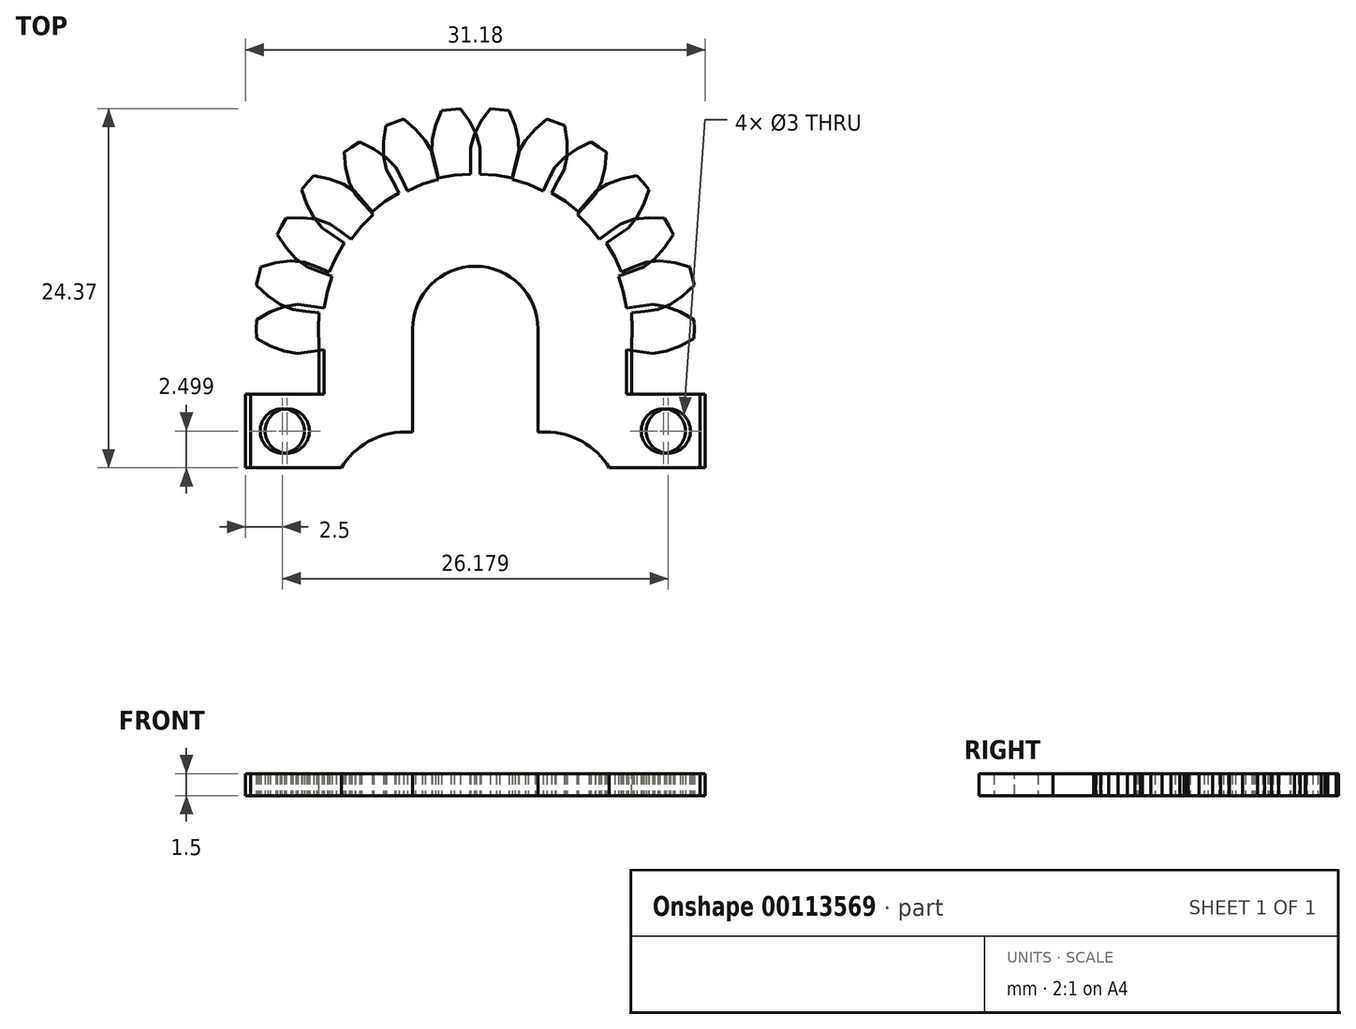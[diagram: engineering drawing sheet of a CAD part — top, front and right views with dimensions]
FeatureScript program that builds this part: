
annotation { "Feature Type Name" : "Feature", "Feature Type Description" : "" }
export const myFeature = defineFeature(function(context is Context, id is Id, definition is map)
    precondition{}
    {
        {
            var Q0;
            Q0=qCreatedBy(makeId("Top.planeOp"),FACE);
            var sketch = newSketch(context, id + "F0", { "sketchPlane" : qUnion([Q0])});
            skLineSegment(sketch, "E0", {"start": v(10.65, 0) * mm, "end": v(10.59, 1.11) * mm});
            skLineSegment(sketch, "E1", {"start": v(10.59, 1.11) * mm, "end": v(11.48, 1.2) * mm});
            skLineSegment(sketch, "E2", {"start": v(11.48, 1.2) * mm, "end": v(12.38, 1.3) * mm});
            skLineSegment(sketch, "E3", {"start": v(12.38, 1.3) * mm, "end": v(13.24, 1.67) * mm});
            skLineSegment(sketch, "E4", {"start": v(13.24, 1.67) * mm, "end": v(14.07, 2.24) * mm});
            skLineSegment(sketch, "E5", {"start": v(14.07, 2.24) * mm, "end": v(14.85, 2.97) * mm});
            skLineSegment(sketch, "E6", {"start": v(14.85, 2.97) * mm, "end": v(14.71, 3.59) * mm});
            skLineSegment(sketch, "E7", {"start": v(14.71, 3.59) * mm, "end": v(14.55, 4.2) * mm});
            skLineSegment(sketch, "E8", {"start": v(14.55, 4.2) * mm, "end": v(13.52, 4.49) * mm});
            skLineSegment(sketch, "E9", {"start": v(13.52, 4.49) * mm, "end": v(12.52, 4.6) * mm});
            skLineSegment(sketch, "E10", {"start": v(12.52, 4.6) * mm, "end": v(11.59, 4.53) * mm});
            skLineSegment(sketch, "E11", {"start": v(11.59, 4.53) * mm, "end": v(10.75, 4.2) * mm});
            skLineSegment(sketch, "E12", {"start": v(10.75, 4.2) * mm, "end": v(9.9, 3.87) * mm});
            skLineSegment(sketch, "E13", {"start": v(9.9, 3.87) * mm, "end": v(9.45, 4.88) * mm});
            skLineSegment(sketch, "E14", {"start": v(9.45, 4.88) * mm, "end": v(8.88, 5.84) * mm});
            skLineSegment(sketch, "E15", {"start": v(8.88, 5.84) * mm, "end": v(9.63, 6.34) * mm});
            skLineSegment(sketch, "E16", {"start": v(9.63, 6.34) * mm, "end": v(10.37, 6.84) * mm});
            skLineSegment(sketch, "E17", {"start": v(10.37, 6.84) * mm, "end": v(10.97, 7.56) * mm});
            skLineSegment(sketch, "E18", {"start": v(10.97, 7.56) * mm, "end": v(11.43, 8.45) * mm});
            skLineSegment(sketch, "E19", {"start": v(11.43, 8.45) * mm, "end": v(11.79, 9.46) * mm});
            skLineSegment(sketch, "E20", {"start": v(11.79, 9.46) * mm, "end": v(11.38, 9.95) * mm});
            skLineSegment(sketch, "E21", {"start": v(11.38, 9.95) * mm, "end": v(10.95, 10.41) * mm});
            skLineSegment(sketch, "E22", {"start": v(10.95, 10.41) * mm, "end": v(9.9, 10.19) * mm});
            skLineSegment(sketch, "E23", {"start": v(9.9, 10.19) * mm, "end": v(8.96, 9.83) * mm});
            skLineSegment(sketch, "E24", {"start": v(8.96, 9.83) * mm, "end": v(8.17, 9.32) * mm});
            skLineSegment(sketch, "E25", {"start": v(8.17, 9.32) * mm, "end": v(7.58, 8.64) * mm});
            skLineSegment(sketch, "E26", {"start": v(7.58, 8.64) * mm, "end": v(7, 7.96) * mm});
            skLineSegment(sketch, "E27", {"start": v(7, 7.96) * mm, "end": v(6.11, 8.64) * mm});
            skLineSegment(sketch, "E28", {"start": v(6.11, 8.64) * mm, "end": v(5.17, 9.22) * mm});
            skLineSegment(sketch, "E29", {"start": v(5.17, 9.22) * mm, "end": v(5.6, 10.01) * mm});
            skLineSegment(sketch, "E30", {"start": v(5.6, 10.01) * mm, "end": v(6.02, 10.8) * mm});
            skLineSegment(sketch, "E31", {"start": v(6.02, 10.8) * mm, "end": v(6.21, 11.72) * mm});
            skLineSegment(sketch, "E32", {"start": v(6.21, 11.72) * mm, "end": v(6.21, 12.73) * mm});
            skLineSegment(sketch, "E33", {"start": v(6.21, 12.73) * mm, "end": v(6.06, 13.79) * mm});
            skLineSegment(sketch, "E34", {"start": v(6.06, 13.79) * mm, "end": v(5.47, 14.03) * mm});
            skLineSegment(sketch, "E35", {"start": v(5.47, 14.03) * mm, "end": v(4.87, 14.24) * mm});
            skLineSegment(sketch, "E36", {"start": v(4.87, 14.24) * mm, "end": v(4.05, 13.55) * mm});
            skLineSegment(sketch, "E37", {"start": v(4.05, 13.55) * mm, "end": v(3.38, 12.8) * mm});
            skLineSegment(sketch, "E38", {"start": v(3.38, 12.8) * mm, "end": v(2.92, 11.98) * mm});
            skLineSegment(sketch, "E39", {"start": v(2.92, 11.98) * mm, "end": v(2.71, 11.1) * mm});
            skLineSegment(sketch, "E40", {"start": v(2.71, 11.1) * mm, "end": v(2.5, 10.23) * mm});
            skLineSegment(sketch, "E41", {"start": v(2.5, 10.23) * mm, "end": v(1.41, 10.42) * mm});
            skLineSegment(sketch, "E42", {"start": v(1.41, 10.42) * mm, "end": v(0.3, 10.5) * mm});
            skLineSegment(sketch, "E43", {"start": v(0.3, 10.5) * mm, "end": v(0.32, 11.4) * mm});
            skLineSegment(sketch, "E44", {"start": v(0.32, 11.4) * mm, "end": v(0.33, 12.3) * mm});
            skLineSegment(sketch, "E45", {"start": v(0.33, 12.3) * mm, "end": v(0.07, 13.2) * mm});
            skLineSegment(sketch, "E46", {"start": v(0.07, 13.2) * mm, "end": v(-0.4, 14.09) * mm});
            skLineSegment(sketch, "E47", {"start": v(-0.4, 14.09) * mm, "end": v(-1.03, 14.95) * mm});
            skLineSegment(sketch, "E48", {"start": v(-1.03, 14.95) * mm, "end": v(-1.66, 14.9) * mm});
            skLineSegment(sketch, "E49", {"start": v(-1.66, 14.9) * mm, "end": v(-2.29, 14.8) * mm});
            skLineSegment(sketch, "E50", {"start": v(-2.29, 14.8) * mm, "end": v(-2.7, 13.81) * mm});
            skLineSegment(sketch, "E51", {"start": v(-2.7, 13.81) * mm, "end": v(-2.93, 12.83) * mm});
            skLineSegment(sketch, "E52", {"start": v(-2.93, 12.83) * mm, "end": v(-2.97, 11.9) * mm});
            skLineSegment(sketch, "E53", {"start": v(-2.97, 11.9) * mm, "end": v(-2.74, 11.03) * mm});
            skLineSegment(sketch, "E54", {"start": v(-2.74, 11.03) * mm, "end": v(-2.52, 10.16) * mm});
            skLineSegment(sketch, "E55", {"start": v(-2.52, 10.16) * mm, "end": v(-3.57, 9.82) * mm});
            skLineSegment(sketch, "E56", {"start": v(-3.57, 9.82) * mm, "end": v(-4.6, 9.37) * mm});
            skLineSegment(sketch, "E57", {"start": v(-4.6, 9.37) * mm, "end": v(-5, 10.17) * mm});
            skLineSegment(sketch, "E58", {"start": v(-5, 10.17) * mm, "end": v(-5.41, 10.97) * mm});
            skLineSegment(sketch, "E59", {"start": v(-5.41, 10.97) * mm, "end": v(-6.05, 11.65) * mm});
            skLineSegment(sketch, "E60", {"start": v(-6.05, 11.65) * mm, "end": v(-6.88, 12.22) * mm});
            skLineSegment(sketch, "E61", {"start": v(-6.88, 12.22) * mm, "end": v(-7.84, 12.7) * mm});
            skLineSegment(sketch, "E62", {"start": v(-7.84, 12.7) * mm, "end": v(-8.37, 12.34) * mm});
            skLineSegment(sketch, "E63", {"start": v(-8.37, 12.34) * mm, "end": v(-8.89, 11.97) * mm});
            skLineSegment(sketch, "E64", {"start": v(-8.89, 11.97) * mm, "end": v(-8.79, 10.9) * mm});
            skLineSegment(sketch, "E65", {"start": v(-8.79, 10.9) * mm, "end": v(-8.55, 9.93) * mm});
            skLineSegment(sketch, "E66", {"start": v(-8.55, 9.93) * mm, "end": v(-8.14, 9.09) * mm});
            skLineSegment(sketch, "E67", {"start": v(-8.14, 9.09) * mm, "end": v(-7.54, 8.42) * mm});
            skLineSegment(sketch, "E68", {"start": v(-7.54, 8.42) * mm, "end": v(-6.93, 7.75) * mm});
            skLineSegment(sketch, "E69", {"start": v(-6.93, 7.75) * mm, "end": v(-7.71, 6.96) * mm});
            skLineSegment(sketch, "E70", {"start": v(-7.71, 6.96) * mm, "end": v(-8.4, 6.1) * mm});
            skLineSegment(sketch, "E71", {"start": v(-8.4, 6.1) * mm, "end": v(-9.14, 6.62) * mm});
            skLineSegment(sketch, "E72", {"start": v(-9.14, 6.62) * mm, "end": v(-9.87, 7.13) * mm});
            skLineSegment(sketch, "E73", {"start": v(-9.87, 7.13) * mm, "end": v(-10.76, 7.43) * mm});
            skLineSegment(sketch, "E74", {"start": v(-10.76, 7.43) * mm, "end": v(-11.76, 7.56) * mm});
            skLineSegment(sketch, "E75", {"start": v(-11.76, 7.56) * mm, "end": v(-12.83, 7.53) * mm});
            skLineSegment(sketch, "E76", {"start": v(-12.83, 7.53) * mm, "end": v(-13.13, 6.97) * mm});
            skLineSegment(sketch, "E77", {"start": v(-13.13, 6.97) * mm, "end": v(-13.42, 6.4) * mm});
            skLineSegment(sketch, "E78", {"start": v(-13.42, 6.4) * mm, "end": v(-12.83, 5.5) * mm});
            skLineSegment(sketch, "E79", {"start": v(-12.83, 5.5) * mm, "end": v(-12.17, 4.75) * mm});
            skLineSegment(sketch, "E80", {"start": v(-12.17, 4.75) * mm, "end": v(-11.41, 4.2) * mm});
            skLineSegment(sketch, "E81", {"start": v(-11.41, 4.2) * mm, "end": v(-10.57, 3.88) * mm});
            skLineSegment(sketch, "E82", {"start": v(-10.57, 3.88) * mm, "end": v(-9.72, 3.58) * mm});
            skLineSegment(sketch, "E83", {"start": v(-9.72, 3.58) * mm, "end": v(-10.05, 2.51) * mm});
            skLineSegment(sketch, "E84", {"start": v(-10.05, 2.51) * mm, "end": v(-10.25, 1.42) * mm});
            skLineSegment(sketch, "E85", {"start": v(-10.25, 1.42) * mm, "end": v(-11.15, 1.54) * mm});
            skLineSegment(sketch, "E86", {"start": v(-11.15, 1.54) * mm, "end": v(-12.04, 1.66) * mm});
            skLineSegment(sketch, "E87", {"start": v(-12.04, 1.66) * mm, "end": v(-12.96, 1.51) * mm});
            skLineSegment(sketch, "E88", {"start": v(-12.96, 1.51) * mm, "end": v(-13.9, 1.16) * mm});
            skLineSegment(sketch, "E89", {"start": v(-13.9, 1.16) * mm, "end": v(-14.84, 0.63) * mm});
            skLineSegment(sketch, "E90", {"start": v(-14.84, 0.63) * mm, "end": v(-14.85, 0) * mm});
            skLineSegment(sketch, "E91", {"start": v(-14.85, 0) * mm, "end": v(-14.84, -0.63) * mm});
            skLineSegment(sketch, "E92", {"start": v(-14.84, -0.63) * mm, "end": v(-13.9, -1.16) * mm});
            skLineSegment(sketch, "E93", {"start": v(-13.9, -1.16) * mm, "end": v(-12.96, -1.51) * mm});
            skLineSegment(sketch, "E94", {"start": v(-12.96, -1.51) * mm, "end": v(-12.04, -1.66) * mm});
            skLineSegment(sketch, "E95", {"start": v(-12.04, -1.66) * mm, "end": v(-11.15, -1.54) * mm});
            skLineSegment(sketch, "E96", {"start": v(-11.15, -1.54) * mm, "end": v(-10.25, -1.42) * mm});
            skLineSegment(sketch, "E97", {"start": v(-10.25, -1.42) * mm, "end": v(-10.05, -2.51) * mm});
            skLineSegment(sketch, "E98", {"start": v(-10.05, -2.51) * mm, "end": v(-9.72, -3.58) * mm});
            skLineSegment(sketch, "E99", {"start": v(-9.72, -3.58) * mm, "end": v(-10.57, -3.88) * mm});
            skLineSegment(sketch, "E100", {"start": v(-10.57, -3.88) * mm, "end": v(-11.41, -4.2) * mm});
            skLineSegment(sketch, "E101", {"start": v(-11.41, -4.2) * mm, "end": v(-12.17, -4.75) * mm});
            skLineSegment(sketch, "E102", {"start": v(-12.17, -4.75) * mm, "end": v(-12.83, -5.5) * mm});
            skLineSegment(sketch, "E103", {"start": v(-12.83, -5.5) * mm, "end": v(-13.42, -6.4) * mm});
            skLineSegment(sketch, "E104", {"start": v(-13.42, -6.4) * mm, "end": v(-13.13, -6.97) * mm});
            skLineSegment(sketch, "E105", {"start": v(-13.13, -6.97) * mm, "end": v(-12.83, -7.53) * mm});
            skLineSegment(sketch, "E106", {"start": v(-12.83, -7.53) * mm, "end": v(-11.76, -7.56) * mm});
            skLineSegment(sketch, "E107", {"start": v(-11.76, -7.56) * mm, "end": v(-10.76, -7.43) * mm});
            skLineSegment(sketch, "E108", {"start": v(-10.76, -7.43) * mm, "end": v(-9.87, -7.13) * mm});
            skLineSegment(sketch, "E109", {"start": v(-9.87, -7.13) * mm, "end": v(-9.14, -6.62) * mm});
            skLineSegment(sketch, "E110", {"start": v(-9.14, -6.62) * mm, "end": v(-8.4, -6.1) * mm});
            skLineSegment(sketch, "E111", {"start": v(-8.4, -6.1) * mm, "end": v(-7.71, -6.96) * mm});
            skLineSegment(sketch, "E112", {"start": v(-7.71, -6.96) * mm, "end": v(-6.93, -7.75) * mm});
            skLineSegment(sketch, "E113", {"start": v(-6.93, -7.75) * mm, "end": v(-7.54, -8.42) * mm});
            skLineSegment(sketch, "E114", {"start": v(-7.54, -8.42) * mm, "end": v(-8.14, -9.09) * mm});
            skLineSegment(sketch, "E115", {"start": v(-8.14, -9.09) * mm, "end": v(-8.55, -9.93) * mm});
            skLineSegment(sketch, "E116", {"start": v(-8.55, -9.93) * mm, "end": v(-8.79, -10.9) * mm});
            skLineSegment(sketch, "E117", {"start": v(-8.79, -10.9) * mm, "end": v(-8.89, -11.97) * mm});
            skLineSegment(sketch, "E118", {"start": v(-8.89, -11.97) * mm, "end": v(-8.37, -12.34) * mm});
            skLineSegment(sketch, "E119", {"start": v(-8.37, -12.34) * mm, "end": v(-7.84, -12.7) * mm});
            skLineSegment(sketch, "E120", {"start": v(-7.84, -12.7) * mm, "end": v(-6.88, -12.22) * mm});
            skLineSegment(sketch, "E121", {"start": v(-6.88, -12.22) * mm, "end": v(-6.05, -11.65) * mm});
            skLineSegment(sketch, "E122", {"start": v(-6.05, -11.65) * mm, "end": v(-5.41, -10.97) * mm});
            skLineSegment(sketch, "E123", {"start": v(-5.41, -10.97) * mm, "end": v(-5, -10.17) * mm});
            skLineSegment(sketch, "E124", {"start": v(-5, -10.17) * mm, "end": v(-4.6, -9.37) * mm});
            skLineSegment(sketch, "E125", {"start": v(-4.6, -9.37) * mm, "end": v(-3.57, -9.82) * mm});
            skLineSegment(sketch, "E126", {"start": v(-3.57, -9.82) * mm, "end": v(-2.52, -10.16) * mm});
            skLineSegment(sketch, "E127", {"start": v(-2.52, -10.16) * mm, "end": v(-2.74, -11.03) * mm});
            skLineSegment(sketch, "E128", {"start": v(-2.74, -11.03) * mm, "end": v(-2.97, -11.9) * mm});
            skLineSegment(sketch, "E129", {"start": v(-2.97, -11.9) * mm, "end": v(-2.93, -12.83) * mm});
            skLineSegment(sketch, "E130", {"start": v(-2.93, -12.83) * mm, "end": v(-2.7, -13.81) * mm});
            skLineSegment(sketch, "E131", {"start": v(-2.7, -13.81) * mm, "end": v(-2.29, -14.8) * mm});
            skLineSegment(sketch, "E132", {"start": v(-2.29, -14.8) * mm, "end": v(-1.66, -14.9) * mm});
            skLineSegment(sketch, "E133", {"start": v(-1.66, -14.9) * mm, "end": v(-1.03, -14.95) * mm});
            skLineSegment(sketch, "E134", {"start": v(-1.03, -14.95) * mm, "end": v(-0.4, -14.09) * mm});
            skLineSegment(sketch, "E135", {"start": v(-0.4, -14.09) * mm, "end": v(0.07, -13.2) * mm});
            skLineSegment(sketch, "E136", {"start": v(0.07, -13.2) * mm, "end": v(0.33, -12.3) * mm});
            skLineSegment(sketch, "E137", {"start": v(0.33, -12.3) * mm, "end": v(0.32, -11.4) * mm});
            skLineSegment(sketch, "E138", {"start": v(0.32, -11.4) * mm, "end": v(0.3, -10.5) * mm});
            skLineSegment(sketch, "E139", {"start": v(0.3, -10.5) * mm, "end": v(1.41, -10.42) * mm});
            skLineSegment(sketch, "E140", {"start": v(1.41, -10.42) * mm, "end": v(2.5, -10.23) * mm});
            skLineSegment(sketch, "E141", {"start": v(2.5, -10.23) * mm, "end": v(2.71, -11.1) * mm});
            skLineSegment(sketch, "E142", {"start": v(2.71, -11.1) * mm, "end": v(2.92, -11.98) * mm});
            skLineSegment(sketch, "E143", {"start": v(2.92, -11.98) * mm, "end": v(3.38, -12.8) * mm});
            skLineSegment(sketch, "E144", {"start": v(3.38, -12.8) * mm, "end": v(4.05, -13.55) * mm});
            skLineSegment(sketch, "E145", {"start": v(4.05, -13.55) * mm, "end": v(4.87, -14.24) * mm});
            skLineSegment(sketch, "E146", {"start": v(4.87, -14.24) * mm, "end": v(5.47, -14.03) * mm});
            skLineSegment(sketch, "E147", {"start": v(5.47, -14.03) * mm, "end": v(6.06, -13.79) * mm});
            skLineSegment(sketch, "E148", {"start": v(6.06, -13.79) * mm, "end": v(6.21, -12.73) * mm});
            skLineSegment(sketch, "E149", {"start": v(6.21, -12.73) * mm, "end": v(6.21, -11.72) * mm});
            skLineSegment(sketch, "E150", {"start": v(6.21, -11.72) * mm, "end": v(6.02, -10.8) * mm});
            skLineSegment(sketch, "E151", {"start": v(6.02, -10.8) * mm, "end": v(5.6, -10.01) * mm});
            skLineSegment(sketch, "E152", {"start": v(5.6, -10.01) * mm, "end": v(5.17, -9.22) * mm});
            skLineSegment(sketch, "E153", {"start": v(5.17, -9.22) * mm, "end": v(6.11, -8.64) * mm});
            skLineSegment(sketch, "E154", {"start": v(6.11, -8.64) * mm, "end": v(7, -7.96) * mm});
            skLineSegment(sketch, "E155", {"start": v(7, -7.96) * mm, "end": v(7.58, -8.64) * mm});
            skLineSegment(sketch, "E156", {"start": v(7.58, -8.64) * mm, "end": v(8.17, -9.32) * mm});
            skLineSegment(sketch, "E157", {"start": v(8.17, -9.32) * mm, "end": v(8.96, -9.83) * mm});
            skLineSegment(sketch, "E158", {"start": v(8.96, -9.83) * mm, "end": v(9.9, -10.19) * mm});
            skLineSegment(sketch, "E159", {"start": v(9.9, -10.19) * mm, "end": v(10.95, -10.41) * mm});
            skLineSegment(sketch, "E160", {"start": v(10.95, -10.41) * mm, "end": v(11.38, -9.95) * mm});
            skLineSegment(sketch, "E161", {"start": v(11.38, -9.95) * mm, "end": v(11.79, -9.46) * mm});
            skLineSegment(sketch, "E162", {"start": v(11.79, -9.46) * mm, "end": v(11.43, -8.45) * mm});
            skLineSegment(sketch, "E163", {"start": v(11.43, -8.45) * mm, "end": v(10.97, -7.56) * mm});
            skLineSegment(sketch, "E164", {"start": v(10.97, -7.56) * mm, "end": v(10.37, -6.84) * mm});
            skLineSegment(sketch, "E165", {"start": v(10.37, -6.84) * mm, "end": v(9.63, -6.34) * mm});
            skLineSegment(sketch, "E166", {"start": v(9.63, -6.34) * mm, "end": v(8.88, -5.84) * mm});
            skLineSegment(sketch, "E167", {"start": v(8.88, -5.84) * mm, "end": v(9.45, -4.88) * mm});
            skLineSegment(sketch, "E168", {"start": v(9.45, -4.88) * mm, "end": v(9.9, -3.87) * mm});
            skLineSegment(sketch, "E169", {"start": v(9.9, -3.87) * mm, "end": v(10.75, -4.2) * mm});
            skLineSegment(sketch, "E170", {"start": v(10.75, -4.2) * mm, "end": v(11.59, -4.53) * mm});
            skLineSegment(sketch, "E171", {"start": v(11.59, -4.53) * mm, "end": v(12.52, -4.6) * mm});
            skLineSegment(sketch, "E172", {"start": v(12.52, -4.6) * mm, "end": v(13.52, -4.49) * mm});
            skLineSegment(sketch, "E173", {"start": v(13.52, -4.49) * mm, "end": v(14.55, -4.2) * mm});
            skLineSegment(sketch, "E174", {"start": v(14.55, -4.2) * mm, "end": v(14.71, -3.59) * mm});
            skLineSegment(sketch, "E175", {"start": v(14.71, -3.59) * mm, "end": v(14.85, -2.97) * mm});
            skLineSegment(sketch, "E176", {"start": v(14.85, -2.97) * mm, "end": v(14.07, -2.24) * mm});
            skLineSegment(sketch, "E177", {"start": v(14.07, -2.24) * mm, "end": v(13.24, -1.67) * mm});
            skLineSegment(sketch, "E178", {"start": v(13.24, -1.67) * mm, "end": v(12.38, -1.3) * mm});
            skLineSegment(sketch, "E179", {"start": v(12.38, -1.3) * mm, "end": v(11.48, -1.2) * mm});
            skLineSegment(sketch, "E180", {"start": v(11.48, -1.2) * mm, "end": v(10.59, -1.11) * mm});
            skLineSegment(sketch, "E181", {"start": v(10.65, 0) * mm, "end": v(10.59, -1.11) * mm});
            skSolve(sketch);
        }
        {
            var Q0;
            Q0=qSketchRegion(id+"F0",true);
            extrude(context, id + "F1", {"entities" : qUnion([Q0]), "depth" : 1.5 * mm});
        }
        {
            var Q0;
            Q0=makeQuery(id+"F1.opExtrude","CAP_FACE",FACE,{"disambiguationData":[OSD([sQuery(id+"F0.wireOp",EDGE,"E0"),sQuery(id+"F0.wireOp",EDGE,"E1"),sQuery(id+"F0.wireOp",EDGE,"E2"),sQuery(id+"F0.wireOp",EDGE,"E3"),sQuery(id+"F0.wireOp",EDGE,"E4"),sQuery(id+"F0.wireOp",EDGE,"E5"),sQuery(id+"F0.wireOp",EDGE,"E6"),sQuery(id+"F0.wireOp",EDGE,"E7"),sQuery(id+"F0.wireOp",EDGE,"E8"),sQuery(id+"F0.wireOp",EDGE,"E9"),sQuery(id+"F0.wireOp",EDGE,"E10"),sQuery(id+"F0.wireOp",EDGE,"E11"),sQuery(id+"F0.wireOp",EDGE,"E12"),sQuery(id+"F0.wireOp",EDGE,"E13"),sQuery(id+"F0.wireOp",EDGE,"E14"),sQuery(id+"F0.wireOp",EDGE,"E15"),sQuery(id+"F0.wireOp",EDGE,"E16"),sQuery(id+"F0.wireOp",EDGE,"E17"),sQuery(id+"F0.wireOp",EDGE,"E18"),sQuery(id+"F0.wireOp",EDGE,"E19"),sQuery(id+"F0.wireOp",EDGE,"E20"),sQuery(id+"F0.wireOp",EDGE,"E21"),sQuery(id+"F0.wireOp",EDGE,"E22"),sQuery(id+"F0.wireOp",EDGE,"E23"),sQuery(id+"F0.wireOp",EDGE,"E24"),sQuery(id+"F0.wireOp",EDGE,"E25"),sQuery(id+"F0.wireOp",EDGE,"E26"),sQuery(id+"F0.wireOp",EDGE,"E27"),sQuery(id+"F0.wireOp",EDGE,"E28"),sQuery(id+"F0.wireOp",EDGE,"E29"),sQuery(id+"F0.wireOp",EDGE,"E30"),sQuery(id+"F0.wireOp",EDGE,"E31"),sQuery(id+"F0.wireOp",EDGE,"E32"),sQuery(id+"F0.wireOp",EDGE,"E33"),sQuery(id+"F0.wireOp",EDGE,"E34"),sQuery(id+"F0.wireOp",EDGE,"E35"),sQuery(id+"F0.wireOp",EDGE,"E36"),sQuery(id+"F0.wireOp",EDGE,"E37"),sQuery(id+"F0.wireOp",EDGE,"E38"),sQuery(id+"F0.wireOp",EDGE,"E39"),sQuery(id+"F0.wireOp",EDGE,"E40"),sQuery(id+"F0.wireOp",EDGE,"E41"),sQuery(id+"F0.wireOp",EDGE,"E42"),sQuery(id+"F0.wireOp",EDGE,"E43"),sQuery(id+"F0.wireOp",EDGE,"E44"),sQuery(id+"F0.wireOp",EDGE,"E45"),sQuery(id+"F0.wireOp",EDGE,"E46"),sQuery(id+"F0.wireOp",EDGE,"E47"),sQuery(id+"F0.wireOp",EDGE,"E48"),sQuery(id+"F0.wireOp",EDGE,"E49"),sQuery(id+"F0.wireOp",EDGE,"E50"),sQuery(id+"F0.wireOp",EDGE,"E51"),sQuery(id+"F0.wireOp",EDGE,"E52"),sQuery(id+"F0.wireOp",EDGE,"E53"),sQuery(id+"F0.wireOp",EDGE,"E54"),sQuery(id+"F0.wireOp",EDGE,"E55"),sQuery(id+"F0.wireOp",EDGE,"E56"),sQuery(id+"F0.wireOp",EDGE,"E57"),sQuery(id+"F0.wireOp",EDGE,"E58"),sQuery(id+"F0.wireOp",EDGE,"E59"),sQuery(id+"F0.wireOp",EDGE,"E60"),sQuery(id+"F0.wireOp",EDGE,"E61"),sQuery(id+"F0.wireOp",EDGE,"E62"),sQuery(id+"F0.wireOp",EDGE,"E63"),sQuery(id+"F0.wireOp",EDGE,"E64"),sQuery(id+"F0.wireOp",EDGE,"E65"),sQuery(id+"F0.wireOp",EDGE,"E66"),sQuery(id+"F0.wireOp",EDGE,"E67"),sQuery(id+"F0.wireOp",EDGE,"E68"),sQuery(id+"F0.wireOp",EDGE,"E69"),sQuery(id+"F0.wireOp",EDGE,"E70"),sQuery(id+"F0.wireOp",EDGE,"E71"),sQuery(id+"F0.wireOp",EDGE,"E72"),sQuery(id+"F0.wireOp",EDGE,"E73"),sQuery(id+"F0.wireOp",EDGE,"E74"),sQuery(id+"F0.wireOp",EDGE,"E75"),sQuery(id+"F0.wireOp",EDGE,"E76"),sQuery(id+"F0.wireOp",EDGE,"E77"),sQuery(id+"F0.wireOp",EDGE,"E78"),sQuery(id+"F0.wireOp",EDGE,"E79"),sQuery(id+"F0.wireOp",EDGE,"E80"),sQuery(id+"F0.wireOp",EDGE,"E81"),sQuery(id+"F0.wireOp",EDGE,"E82"),sQuery(id+"F0.wireOp",EDGE,"E83"),sQuery(id+"F0.wireOp",EDGE,"E84"),sQuery(id+"F0.wireOp",EDGE,"E85"),sQuery(id+"F0.wireOp",EDGE,"E86"),sQuery(id+"F0.wireOp",EDGE,"E87"),sQuery(id+"F0.wireOp",EDGE,"E88"),sQuery(id+"F0.wireOp",EDGE,"E89"),sQuery(id+"F0.wireOp",EDGE,"E90"),sQuery(id+"F0.wireOp",EDGE,"E91"),sQuery(id+"F0.wireOp",EDGE,"E92"),sQuery(id+"F0.wireOp",EDGE,"E93"),sQuery(id+"F0.wireOp",EDGE,"E94"),sQuery(id+"F0.wireOp",EDGE,"E95"),sQuery(id+"F0.wireOp",EDGE,"E96"),sQuery(id+"F0.wireOp",EDGE,"E97"),sQuery(id+"F0.wireOp",EDGE,"E98"),sQuery(id+"F0.wireOp",EDGE,"E99"),sQuery(id+"F0.wireOp",EDGE,"E100"),sQuery(id+"F0.wireOp",EDGE,"E101"),sQuery(id+"F0.wireOp",EDGE,"E102"),sQuery(id+"F0.wireOp",EDGE,"E103"),sQuery(id+"F0.wireOp",EDGE,"E104"),sQuery(id+"F0.wireOp",EDGE,"E105"),sQuery(id+"F0.wireOp",EDGE,"E106"),sQuery(id+"F0.wireOp",EDGE,"E107"),sQuery(id+"F0.wireOp",EDGE,"E108"),sQuery(id+"F0.wireOp",EDGE,"E109"),sQuery(id+"F0.wireOp",EDGE,"E110"),sQuery(id+"F0.wireOp",EDGE,"E111"),sQuery(id+"F0.wireOp",EDGE,"E112"),sQuery(id+"F0.wireOp",EDGE,"E113"),sQuery(id+"F0.wireOp",EDGE,"E114"),sQuery(id+"F0.wireOp",EDGE,"E115"),sQuery(id+"F0.wireOp",EDGE,"E116"),sQuery(id+"F0.wireOp",EDGE,"E117"),sQuery(id+"F0.wireOp",EDGE,"E118"),sQuery(id+"F0.wireOp",EDGE,"E119"),sQuery(id+"F0.wireOp",EDGE,"E120"),sQuery(id+"F0.wireOp",EDGE,"E121"),sQuery(id+"F0.wireOp",EDGE,"E122"),sQuery(id+"F0.wireOp",EDGE,"E123"),sQuery(id+"F0.wireOp",EDGE,"E124"),sQuery(id+"F0.wireOp",EDGE,"E125"),sQuery(id+"F0.wireOp",EDGE,"E126"),sQuery(id+"F0.wireOp",EDGE,"E127"),sQuery(id+"F0.wireOp",EDGE,"E128"),sQuery(id+"F0.wireOp",EDGE,"E129"),sQuery(id+"F0.wireOp",EDGE,"E130"),sQuery(id+"F0.wireOp",EDGE,"E131"),sQuery(id+"F0.wireOp",EDGE,"E132"),sQuery(id+"F0.wireOp",EDGE,"E133"),sQuery(id+"F0.wireOp",EDGE,"E134"),sQuery(id+"F0.wireOp",EDGE,"E135"),sQuery(id+"F0.wireOp",EDGE,"E136"),sQuery(id+"F0.wireOp",EDGE,"E137"),sQuery(id+"F0.wireOp",EDGE,"E138"),sQuery(id+"F0.wireOp",EDGE,"E139"),sQuery(id+"F0.wireOp",EDGE,"E140"),sQuery(id+"F0.wireOp",EDGE,"E141"),sQuery(id+"F0.wireOp",EDGE,"E142"),sQuery(id+"F0.wireOp",EDGE,"E143"),sQuery(id+"F0.wireOp",EDGE,"E144"),sQuery(id+"F0.wireOp",EDGE,"E145"),sQuery(id+"F0.wireOp",EDGE,"E146"),sQuery(id+"F0.wireOp",EDGE,"E147"),sQuery(id+"F0.wireOp",EDGE,"E148"),sQuery(id+"F0.wireOp",EDGE,"E149"),sQuery(id+"F0.wireOp",EDGE,"E150"),sQuery(id+"F0.wireOp",EDGE,"E151"),sQuery(id+"F0.wireOp",EDGE,"E152"),sQuery(id+"F0.wireOp",EDGE,"E153"),sQuery(id+"F0.wireOp",EDGE,"E154"),sQuery(id+"F0.wireOp",EDGE,"E155"),sQuery(id+"F0.wireOp",EDGE,"E156"),sQuery(id+"F0.wireOp",EDGE,"E157"),sQuery(id+"F0.wireOp",EDGE,"E158"),sQuery(id+"F0.wireOp",EDGE,"E159"),sQuery(id+"F0.wireOp",EDGE,"E160"),sQuery(id+"F0.wireOp",EDGE,"E161"),sQuery(id+"F0.wireOp",EDGE,"E162"),sQuery(id+"F0.wireOp",EDGE,"E163"),sQuery(id+"F0.wireOp",EDGE,"E164"),sQuery(id+"F0.wireOp",EDGE,"E165"),sQuery(id+"F0.wireOp",EDGE,"E166"),sQuery(id+"F0.wireOp",EDGE,"E167"),sQuery(id+"F0.wireOp",EDGE,"E168"),sQuery(id+"F0.wireOp",EDGE,"E169"),sQuery(id+"F0.wireOp",EDGE,"E170"),sQuery(id+"F0.wireOp",EDGE,"E171"),sQuery(id+"F0.wireOp",EDGE,"E172"),sQuery(id+"F0.wireOp",EDGE,"E173"),sQuery(id+"F0.wireOp",EDGE,"E174"),sQuery(id+"F0.wireOp",EDGE,"E175"),sQuery(id+"F0.wireOp",EDGE,"E176"),sQuery(id+"F0.wireOp",EDGE,"E177"),sQuery(id+"F0.wireOp",EDGE,"E178"),sQuery(id+"F0.wireOp",EDGE,"E179"),sQuery(id+"F0.wireOp",EDGE,"E180"),sQuery(id+"F0.wireOp",EDGE,"E181")])],"isStart":false});
            var sketch = newSketch(context, id + "F2", { "sketchPlane" : qUnion([Q0])});
            skArc(sketch, "E182", {"start": v(4.25, 0) * mm, "mid": v(0, 4.25) * mm, "end": v(-4.25, 0) * mm});
            skLineSegment(sketch, "E183", {"start": v(-10.25, -1.42) * mm, "end": v(-4.25, -1.42) * mm});
            skLineSegment(sketch, "E184.0", {"start": v(10.65, 0) * mm, "end": v(10.59, -1.11) * mm});
            skLineSegment(sketch, "E185", {"start": v(10.59, -1.11) * mm, "end": v(10.59, -1.42) * mm});
            skLineSegment(sketch, "E186", {"start": v(-4.25, 0) * mm, "end": v(-4.25, -1.42) * mm});
            skLineSegment(sketch, "E187.MirrorCS", {"start": v(4.25, 0) * mm, "end": v(4.25, -1.42) * mm});
            skLineSegment(sketch, "E188.trimOffspring", {"start": v(4.25, -1.42) * mm, "end": v(10.59, -1.42) * mm});
            skSolve(sketch);
        }
        {
            var Q0;
            Q0=makeQuery(id+"F2.imprint","IMPRINT",FACE,{"disambiguationData":[TD([[makeQuery(id+"F2.imprint","IMPRINT",EDGE,{"derivedFrom":sQuery(id+"F2.wireOp",EDGE,"E182")}),1.0]])]});
            extrude(context, id + "F3", {"entities" : qUnion([Q0]), "operationType" : NewBodyOperationType.REMOVE, "endBound" : BoundingType.UP_TO_NEXT, "oppositeDirection" : true, "depth" : 25 * mm});
        }
        {
            var Q0;
            Q0=makeQuery(id+"F3.boolean.opBoolean","COPY",FACE,{"derivedFrom":makeQuery(id+"F3.opExtrude","SWEPT_FACE",FACE,{"disambiguationData":[OSD([sQuery(id+"F2.wireOp",EDGE,"E183")])]})});
            var sketch = newSketch(context, id + "F4", { "sketchPlane" : qUnion([Q0])});
            skLineSegment(sketch, "E189.bottom", {"start": v(-10.25, 1.5) * mm, "end": v(-4.25, 1.5) * mm});
            skLineSegment(sketch, "E189.top", {"start": v(-10.25, 0) * mm, "end": v(-4.25, 0) * mm});
            skLineSegment(sketch, "E189.left", {"start": v(-10.25, 1.5) * mm, "end": v(-10.25, 0) * mm});
            skLineSegment(sketch, "E189.right", {"start": v(-4.25, 1.5) * mm, "end": v(-4.25, 0) * mm});
            skLineSegment(sketch, "E190.0", {"start": v(4.25, 1.5) * mm, "end": v(10.59, 1.5) * mm});
            skLineSegment(sketch, "E191.0", {"start": v(4.25, 0) * mm, "end": v(4.25, 1.5) * mm});
            skLineSegment(sketch, "E192.0.0", {"start": v(10.59, 0) * mm, "end": v(10.59, 1.5) * mm});
            skLineSegment(sketch, "E192.0.1", {"start": v(10.59, 1.5) * mm, "end": v(4.25, 1.5) * mm});
            skLineSegment(sketch, "E192.0.2", {"start": v(4.25, 1.5) * mm, "end": v(4.25, 0) * mm});
            skLineSegment(sketch, "E192.0.3", {"start": v(4.25, 0) * mm, "end": v(10.59, 0) * mm});
            skSolve(sketch);
        }
        {
            var Q0;
            Q0=qSketchRegion(id+"F4",true);
            extrude(context, id + "F5", {"entities" : qUnion([Q0]), "operationType" : NewBodyOperationType.ADD, "depth" : 8 * mm});
        }
        {
            var Q0;
            Q0=makeQuery(id+"F5.boolean.opBoolean","MERGE",FACE,{"derivedFrom":[makeQuery(id+"F3.boolean.opBoolean","COPY",FACE,{"derivedFrom":makeQuery(id+"F3.opExtrude","SWEPT_FACE",FACE,{"disambiguationData":[OSD([sQuery(id+"F2.wireOp",EDGE,"E185")])]})}),makeQuery(id+"F5.opExtrude","SWEPT_FACE",FACE,{"disambiguationData":[OSD([sQuery(id+"F4.wireOp",EDGE,"E192.0.0")])]})]});
            var sketch = newSketch(context, id + "F6", { "sketchPlane" : qUnion([Q0])});
            skLineSegment(sketch, "E193.bottom", {"start": v(-9.42, 0) * mm, "end": v(-4.42, 0) * mm});
            skLineSegment(sketch, "E193.top", {"start": v(-9.42, 1.5) * mm, "end": v(-4.42, 1.5) * mm});
            skLineSegment(sketch, "E193.left", {"start": v(-9.42, 0) * mm, "end": v(-9.42, 1.5) * mm});
            skLineSegment(sketch, "E193.right", {"start": v(-4.42, 0) * mm, "end": v(-4.42, 1.5) * mm});
            skSolve(sketch);
        }
        {
            var Q0;
            Q0=qSketchRegion(id+"F6",true);
            extrude(context, id + "F7", {"entities" : qUnion([Q0]), "operationType" : NewBodyOperationType.ADD, "depth" : 5 * mm});
        }
        {
            var Q0;
            Q0=makeQuery(id+"F7.boolean.opBoolean","MERGE",FACE,{"derivedFrom":[makeQuery(id+"F5.boolean.opBoolean","MERGE",FACE,{"derivedFrom":[makeQuery(id+"F1.opExtrude","CAP_FACE",FACE,{"disambiguationData":[OSD([sQuery(id+"F0.wireOp",EDGE,"E0"),sQuery(id+"F0.wireOp",EDGE,"E1"),sQuery(id+"F0.wireOp",EDGE,"E2"),sQuery(id+"F0.wireOp",EDGE,"E3"),sQuery(id+"F0.wireOp",EDGE,"E4"),sQuery(id+"F0.wireOp",EDGE,"E5"),sQuery(id+"F0.wireOp",EDGE,"E6"),sQuery(id+"F0.wireOp",EDGE,"E7"),sQuery(id+"F0.wireOp",EDGE,"E8"),sQuery(id+"F0.wireOp",EDGE,"E9"),sQuery(id+"F0.wireOp",EDGE,"E10"),sQuery(id+"F0.wireOp",EDGE,"E11"),sQuery(id+"F0.wireOp",EDGE,"E12"),sQuery(id+"F0.wireOp",EDGE,"E13"),sQuery(id+"F0.wireOp",EDGE,"E14"),sQuery(id+"F0.wireOp",EDGE,"E15"),sQuery(id+"F0.wireOp",EDGE,"E16"),sQuery(id+"F0.wireOp",EDGE,"E17"),sQuery(id+"F0.wireOp",EDGE,"E18"),sQuery(id+"F0.wireOp",EDGE,"E19"),sQuery(id+"F0.wireOp",EDGE,"E20"),sQuery(id+"F0.wireOp",EDGE,"E21"),sQuery(id+"F0.wireOp",EDGE,"E22"),sQuery(id+"F0.wireOp",EDGE,"E23"),sQuery(id+"F0.wireOp",EDGE,"E24"),sQuery(id+"F0.wireOp",EDGE,"E25"),sQuery(id+"F0.wireOp",EDGE,"E26"),sQuery(id+"F0.wireOp",EDGE,"E27"),sQuery(id+"F0.wireOp",EDGE,"E28"),sQuery(id+"F0.wireOp",EDGE,"E29"),sQuery(id+"F0.wireOp",EDGE,"E30"),sQuery(id+"F0.wireOp",EDGE,"E31"),sQuery(id+"F0.wireOp",EDGE,"E32"),sQuery(id+"F0.wireOp",EDGE,"E33"),sQuery(id+"F0.wireOp",EDGE,"E34"),sQuery(id+"F0.wireOp",EDGE,"E35"),sQuery(id+"F0.wireOp",EDGE,"E36"),sQuery(id+"F0.wireOp",EDGE,"E37"),sQuery(id+"F0.wireOp",EDGE,"E38"),sQuery(id+"F0.wireOp",EDGE,"E39"),sQuery(id+"F0.wireOp",EDGE,"E40"),sQuery(id+"F0.wireOp",EDGE,"E41"),sQuery(id+"F0.wireOp",EDGE,"E42"),sQuery(id+"F0.wireOp",EDGE,"E43"),sQuery(id+"F0.wireOp",EDGE,"E44"),sQuery(id+"F0.wireOp",EDGE,"E45"),sQuery(id+"F0.wireOp",EDGE,"E46"),sQuery(id+"F0.wireOp",EDGE,"E47"),sQuery(id+"F0.wireOp",EDGE,"E48"),sQuery(id+"F0.wireOp",EDGE,"E49"),sQuery(id+"F0.wireOp",EDGE,"E50"),sQuery(id+"F0.wireOp",EDGE,"E51"),sQuery(id+"F0.wireOp",EDGE,"E52"),sQuery(id+"F0.wireOp",EDGE,"E53"),sQuery(id+"F0.wireOp",EDGE,"E54"),sQuery(id+"F0.wireOp",EDGE,"E55"),sQuery(id+"F0.wireOp",EDGE,"E56"),sQuery(id+"F0.wireOp",EDGE,"E57"),sQuery(id+"F0.wireOp",EDGE,"E58"),sQuery(id+"F0.wireOp",EDGE,"E59"),sQuery(id+"F0.wireOp",EDGE,"E60"),sQuery(id+"F0.wireOp",EDGE,"E61"),sQuery(id+"F0.wireOp",EDGE,"E62"),sQuery(id+"F0.wireOp",EDGE,"E63"),sQuery(id+"F0.wireOp",EDGE,"E64"),sQuery(id+"F0.wireOp",EDGE,"E65"),sQuery(id+"F0.wireOp",EDGE,"E66"),sQuery(id+"F0.wireOp",EDGE,"E67"),sQuery(id+"F0.wireOp",EDGE,"E68"),sQuery(id+"F0.wireOp",EDGE,"E69"),sQuery(id+"F0.wireOp",EDGE,"E70"),sQuery(id+"F0.wireOp",EDGE,"E71"),sQuery(id+"F0.wireOp",EDGE,"E72"),sQuery(id+"F0.wireOp",EDGE,"E73"),sQuery(id+"F0.wireOp",EDGE,"E74"),sQuery(id+"F0.wireOp",EDGE,"E75"),sQuery(id+"F0.wireOp",EDGE,"E76"),sQuery(id+"F0.wireOp",EDGE,"E77"),sQuery(id+"F0.wireOp",EDGE,"E78"),sQuery(id+"F0.wireOp",EDGE,"E79"),sQuery(id+"F0.wireOp",EDGE,"E80"),sQuery(id+"F0.wireOp",EDGE,"E81"),sQuery(id+"F0.wireOp",EDGE,"E82"),sQuery(id+"F0.wireOp",EDGE,"E83"),sQuery(id+"F0.wireOp",EDGE,"E84"),sQuery(id+"F0.wireOp",EDGE,"E85"),sQuery(id+"F0.wireOp",EDGE,"E86"),sQuery(id+"F0.wireOp",EDGE,"E87"),sQuery(id+"F0.wireOp",EDGE,"E88"),sQuery(id+"F0.wireOp",EDGE,"E89"),sQuery(id+"F0.wireOp",EDGE,"E90"),sQuery(id+"F0.wireOp",EDGE,"E91"),sQuery(id+"F0.wireOp",EDGE,"E92"),sQuery(id+"F0.wireOp",EDGE,"E93"),sQuery(id+"F0.wireOp",EDGE,"E94"),sQuery(id+"F0.wireOp",EDGE,"E95"),sQuery(id+"F0.wireOp",EDGE,"E96"),sQuery(id+"F0.wireOp",EDGE,"E97"),sQuery(id+"F0.wireOp",EDGE,"E98"),sQuery(id+"F0.wireOp",EDGE,"E99"),sQuery(id+"F0.wireOp",EDGE,"E100"),sQuery(id+"F0.wireOp",EDGE,"E101"),sQuery(id+"F0.wireOp",EDGE,"E102"),sQuery(id+"F0.wireOp",EDGE,"E103"),sQuery(id+"F0.wireOp",EDGE,"E104"),sQuery(id+"F0.wireOp",EDGE,"E105"),sQuery(id+"F0.wireOp",EDGE,"E106"),sQuery(id+"F0.wireOp",EDGE,"E107"),sQuery(id+"F0.wireOp",EDGE,"E108"),sQuery(id+"F0.wireOp",EDGE,"E109"),sQuery(id+"F0.wireOp",EDGE,"E110"),sQuery(id+"F0.wireOp",EDGE,"E111"),sQuery(id+"F0.wireOp",EDGE,"E112"),sQuery(id+"F0.wireOp",EDGE,"E113"),sQuery(id+"F0.wireOp",EDGE,"E114"),sQuery(id+"F0.wireOp",EDGE,"E115"),sQuery(id+"F0.wireOp",EDGE,"E116"),sQuery(id+"F0.wireOp",EDGE,"E117"),sQuery(id+"F0.wireOp",EDGE,"E118"),sQuery(id+"F0.wireOp",EDGE,"E119"),sQuery(id+"F0.wireOp",EDGE,"E120"),sQuery(id+"F0.wireOp",EDGE,"E121"),sQuery(id+"F0.wireOp",EDGE,"E122"),sQuery(id+"F0.wireOp",EDGE,"E123"),sQuery(id+"F0.wireOp",EDGE,"E124"),sQuery(id+"F0.wireOp",EDGE,"E125"),sQuery(id+"F0.wireOp",EDGE,"E126"),sQuery(id+"F0.wireOp",EDGE,"E127"),sQuery(id+"F0.wireOp",EDGE,"E128"),sQuery(id+"F0.wireOp",EDGE,"E129"),sQuery(id+"F0.wireOp",EDGE,"E130"),sQuery(id+"F0.wireOp",EDGE,"E131"),sQuery(id+"F0.wireOp",EDGE,"E132"),sQuery(id+"F0.wireOp",EDGE,"E133"),sQuery(id+"F0.wireOp",EDGE,"E134"),sQuery(id+"F0.wireOp",EDGE,"E135"),sQuery(id+"F0.wireOp",EDGE,"E136"),sQuery(id+"F0.wireOp",EDGE,"E137"),sQuery(id+"F0.wireOp",EDGE,"E138"),sQuery(id+"F0.wireOp",EDGE,"E139"),sQuery(id+"F0.wireOp",EDGE,"E140"),sQuery(id+"F0.wireOp",EDGE,"E141"),sQuery(id+"F0.wireOp",EDGE,"E142"),sQuery(id+"F0.wireOp",EDGE,"E143"),sQuery(id+"F0.wireOp",EDGE,"E144"),sQuery(id+"F0.wireOp",EDGE,"E145"),sQuery(id+"F0.wireOp",EDGE,"E146"),sQuery(id+"F0.wireOp",EDGE,"E147"),sQuery(id+"F0.wireOp",EDGE,"E148"),sQuery(id+"F0.wireOp",EDGE,"E149"),sQuery(id+"F0.wireOp",EDGE,"E150"),sQuery(id+"F0.wireOp",EDGE,"E151"),sQuery(id+"F0.wireOp",EDGE,"E152"),sQuery(id+"F0.wireOp",EDGE,"E153"),sQuery(id+"F0.wireOp",EDGE,"E154"),sQuery(id+"F0.wireOp",EDGE,"E155"),sQuery(id+"F0.wireOp",EDGE,"E156"),sQuery(id+"F0.wireOp",EDGE,"E157"),sQuery(id+"F0.wireOp",EDGE,"E158"),sQuery(id+"F0.wireOp",EDGE,"E159"),sQuery(id+"F0.wireOp",EDGE,"E160"),sQuery(id+"F0.wireOp",EDGE,"E161"),sQuery(id+"F0.wireOp",EDGE,"E162"),sQuery(id+"F0.wireOp",EDGE,"E163"),sQuery(id+"F0.wireOp",EDGE,"E164"),sQuery(id+"F0.wireOp",EDGE,"E165"),sQuery(id+"F0.wireOp",EDGE,"E166"),sQuery(id+"F0.wireOp",EDGE,"E167"),sQuery(id+"F0.wireOp",EDGE,"E168"),sQuery(id+"F0.wireOp",EDGE,"E169"),sQuery(id+"F0.wireOp",EDGE,"E170"),sQuery(id+"F0.wireOp",EDGE,"E171"),sQuery(id+"F0.wireOp",EDGE,"E172"),sQuery(id+"F0.wireOp",EDGE,"E173"),sQuery(id+"F0.wireOp",EDGE,"E174"),sQuery(id+"F0.wireOp",EDGE,"E175"),sQuery(id+"F0.wireOp",EDGE,"E176"),sQuery(id+"F0.wireOp",EDGE,"E177"),sQuery(id+"F0.wireOp",EDGE,"E178"),sQuery(id+"F0.wireOp",EDGE,"E179"),sQuery(id+"F0.wireOp",EDGE,"E180"),sQuery(id+"F0.wireOp",EDGE,"E181")])],"isStart":true}),makeQuery(id+"F5.opExtrude","SWEPT_FACE",FACE,{"disambiguationData":[OSD([sQuery(id+"F4.wireOp",EDGE,"E189.top")])]}),makeQuery(id+"F5.opExtrude","SWEPT_FACE",FACE,{"disambiguationData":[OSD([sQuery(id+"F4.wireOp",EDGE,"E192.0.3")])]})]}),makeQuery(id+"F7.opExtrude","SWEPT_FACE",FACE,{"disambiguationData":[OSD([sQuery(id+"F6.wireOp",EDGE,"E193.bottom")])]})]});
            var sketch = newSketch(context, id + "F8", { "sketchPlane" : qUnion([Q0])});
            skCircle(sketch, "E194", {"center": v(13.09, 6.92) * mm, "radius": 1.5 * mm});
            skPoint(sketch, "E195", {"position": v(15.59, 6.92) * mm});
            skPoint(sketch, "E196", {"position": v(13.09, 4.42) * mm});
            skSolve(sketch);
        }
        {
            var Q0;
            Q0=qSketchRegion(id+"F8",true);
            extrude(context, id + "F9", {"entities" : qUnion([Q0]), "operationType" : NewBodyOperationType.REMOVE, "endBound" : BoundingType.UP_TO_NEXT, "oppositeDirection" : true, "depth" : 25 * mm});
        }
        {
            var Q0;
            Q0=qCreatedBy(makeId("Top.planeOp"),FACE);
            var sketch = newSketch(context, id + "F10", { "sketchPlane" : qUnion([Q0])});
            skLineSegment(sketch, "E197.0", {"start": v(-10.25, -9.42) * mm, "end": v(-10.25, -1.42) * mm, "construction": true});
            skLineSegment(sketch, "E198.bottom", {"start": v(-10.25, -9.42) * mm, "end": v(-15.25, -9.42) * mm});
            skLineSegment(sketch, "E198.top", {"start": v(-10.25, -4.42) * mm, "end": v(-15.25, -4.42) * mm});
            skLineSegment(sketch, "E198.left", {"start": v(-10.25, -9.42) * mm, "end": v(-10.25, -4.42) * mm});
            skLineSegment(sketch, "E198.right", {"start": v(-15.25, -9.42) * mm, "end": v(-15.25, -4.42) * mm});
            skCircle(sketch, "E199", {"center": v(-12.75, -6.92) * mm, "radius": 1.5 * mm});
            skPoint(sketch, "E199.centerSnap0", {"position": v(-12.75, -9.42) * mm});
            skPoint(sketch, "E199.centerSnap1", {"position": v(-10.25, -6.92) * mm});
            skSolve(sketch);
        }
        {
            var Q0;
            Q0=qSketchRegion(id+"F10",true);
            extrude(context, id + "F11", {"entities" : qUnion([Q0]), "operationType" : NewBodyOperationType.ADD, "depth" : 1.5 * mm});
        }
        {
            var Q0;
            Q0=makeQuery(id+"F11.boolean.opBoolean","MERGE",FACE,{"derivedFrom":[makeQuery(id+"F7.boolean.opBoolean","MERGE",FACE,{"derivedFrom":[makeQuery(id+"F5.boolean.opBoolean","MERGE",FACE,{"derivedFrom":[makeQuery(id+"F1.opExtrude","CAP_FACE",FACE,{"disambiguationData":[OSD([sQuery(id+"F0.wireOp",EDGE,"E0"),sQuery(id+"F0.wireOp",EDGE,"E1"),sQuery(id+"F0.wireOp",EDGE,"E2"),sQuery(id+"F0.wireOp",EDGE,"E3"),sQuery(id+"F0.wireOp",EDGE,"E4"),sQuery(id+"F0.wireOp",EDGE,"E5"),sQuery(id+"F0.wireOp",EDGE,"E6"),sQuery(id+"F0.wireOp",EDGE,"E7"),sQuery(id+"F0.wireOp",EDGE,"E8"),sQuery(id+"F0.wireOp",EDGE,"E9"),sQuery(id+"F0.wireOp",EDGE,"E10"),sQuery(id+"F0.wireOp",EDGE,"E11"),sQuery(id+"F0.wireOp",EDGE,"E12"),sQuery(id+"F0.wireOp",EDGE,"E13"),sQuery(id+"F0.wireOp",EDGE,"E14"),sQuery(id+"F0.wireOp",EDGE,"E15"),sQuery(id+"F0.wireOp",EDGE,"E16"),sQuery(id+"F0.wireOp",EDGE,"E17"),sQuery(id+"F0.wireOp",EDGE,"E18"),sQuery(id+"F0.wireOp",EDGE,"E19"),sQuery(id+"F0.wireOp",EDGE,"E20"),sQuery(id+"F0.wireOp",EDGE,"E21"),sQuery(id+"F0.wireOp",EDGE,"E22"),sQuery(id+"F0.wireOp",EDGE,"E23"),sQuery(id+"F0.wireOp",EDGE,"E24"),sQuery(id+"F0.wireOp",EDGE,"E25"),sQuery(id+"F0.wireOp",EDGE,"E26"),sQuery(id+"F0.wireOp",EDGE,"E27"),sQuery(id+"F0.wireOp",EDGE,"E28"),sQuery(id+"F0.wireOp",EDGE,"E29"),sQuery(id+"F0.wireOp",EDGE,"E30"),sQuery(id+"F0.wireOp",EDGE,"E31"),sQuery(id+"F0.wireOp",EDGE,"E32"),sQuery(id+"F0.wireOp",EDGE,"E33"),sQuery(id+"F0.wireOp",EDGE,"E34"),sQuery(id+"F0.wireOp",EDGE,"E35"),sQuery(id+"F0.wireOp",EDGE,"E36"),sQuery(id+"F0.wireOp",EDGE,"E37"),sQuery(id+"F0.wireOp",EDGE,"E38"),sQuery(id+"F0.wireOp",EDGE,"E39"),sQuery(id+"F0.wireOp",EDGE,"E40"),sQuery(id+"F0.wireOp",EDGE,"E41"),sQuery(id+"F0.wireOp",EDGE,"E42"),sQuery(id+"F0.wireOp",EDGE,"E43"),sQuery(id+"F0.wireOp",EDGE,"E44"),sQuery(id+"F0.wireOp",EDGE,"E45"),sQuery(id+"F0.wireOp",EDGE,"E46"),sQuery(id+"F0.wireOp",EDGE,"E47"),sQuery(id+"F0.wireOp",EDGE,"E48"),sQuery(id+"F0.wireOp",EDGE,"E49"),sQuery(id+"F0.wireOp",EDGE,"E50"),sQuery(id+"F0.wireOp",EDGE,"E51"),sQuery(id+"F0.wireOp",EDGE,"E52"),sQuery(id+"F0.wireOp",EDGE,"E53"),sQuery(id+"F0.wireOp",EDGE,"E54"),sQuery(id+"F0.wireOp",EDGE,"E55"),sQuery(id+"F0.wireOp",EDGE,"E56"),sQuery(id+"F0.wireOp",EDGE,"E57"),sQuery(id+"F0.wireOp",EDGE,"E58"),sQuery(id+"F0.wireOp",EDGE,"E59"),sQuery(id+"F0.wireOp",EDGE,"E60"),sQuery(id+"F0.wireOp",EDGE,"E61"),sQuery(id+"F0.wireOp",EDGE,"E62"),sQuery(id+"F0.wireOp",EDGE,"E63"),sQuery(id+"F0.wireOp",EDGE,"E64"),sQuery(id+"F0.wireOp",EDGE,"E65"),sQuery(id+"F0.wireOp",EDGE,"E66"),sQuery(id+"F0.wireOp",EDGE,"E67"),sQuery(id+"F0.wireOp",EDGE,"E68"),sQuery(id+"F0.wireOp",EDGE,"E69"),sQuery(id+"F0.wireOp",EDGE,"E70"),sQuery(id+"F0.wireOp",EDGE,"E71"),sQuery(id+"F0.wireOp",EDGE,"E72"),sQuery(id+"F0.wireOp",EDGE,"E73"),sQuery(id+"F0.wireOp",EDGE,"E74"),sQuery(id+"F0.wireOp",EDGE,"E75"),sQuery(id+"F0.wireOp",EDGE,"E76"),sQuery(id+"F0.wireOp",EDGE,"E77"),sQuery(id+"F0.wireOp",EDGE,"E78"),sQuery(id+"F0.wireOp",EDGE,"E79"),sQuery(id+"F0.wireOp",EDGE,"E80"),sQuery(id+"F0.wireOp",EDGE,"E81"),sQuery(id+"F0.wireOp",EDGE,"E82"),sQuery(id+"F0.wireOp",EDGE,"E83"),sQuery(id+"F0.wireOp",EDGE,"E84"),sQuery(id+"F0.wireOp",EDGE,"E85"),sQuery(id+"F0.wireOp",EDGE,"E86"),sQuery(id+"F0.wireOp",EDGE,"E87"),sQuery(id+"F0.wireOp",EDGE,"E88"),sQuery(id+"F0.wireOp",EDGE,"E89"),sQuery(id+"F0.wireOp",EDGE,"E90"),sQuery(id+"F0.wireOp",EDGE,"E91"),sQuery(id+"F0.wireOp",EDGE,"E92"),sQuery(id+"F0.wireOp",EDGE,"E93"),sQuery(id+"F0.wireOp",EDGE,"E94"),sQuery(id+"F0.wireOp",EDGE,"E95"),sQuery(id+"F0.wireOp",EDGE,"E96"),sQuery(id+"F0.wireOp",EDGE,"E97"),sQuery(id+"F0.wireOp",EDGE,"E98"),sQuery(id+"F0.wireOp",EDGE,"E99"),sQuery(id+"F0.wireOp",EDGE,"E100"),sQuery(id+"F0.wireOp",EDGE,"E101"),sQuery(id+"F0.wireOp",EDGE,"E102"),sQuery(id+"F0.wireOp",EDGE,"E103"),sQuery(id+"F0.wireOp",EDGE,"E104"),sQuery(id+"F0.wireOp",EDGE,"E105"),sQuery(id+"F0.wireOp",EDGE,"E106"),sQuery(id+"F0.wireOp",EDGE,"E107"),sQuery(id+"F0.wireOp",EDGE,"E108"),sQuery(id+"F0.wireOp",EDGE,"E109"),sQuery(id+"F0.wireOp",EDGE,"E110"),sQuery(id+"F0.wireOp",EDGE,"E111"),sQuery(id+"F0.wireOp",EDGE,"E112"),sQuery(id+"F0.wireOp",EDGE,"E113"),sQuery(id+"F0.wireOp",EDGE,"E114"),sQuery(id+"F0.wireOp",EDGE,"E115"),sQuery(id+"F0.wireOp",EDGE,"E116"),sQuery(id+"F0.wireOp",EDGE,"E117"),sQuery(id+"F0.wireOp",EDGE,"E118"),sQuery(id+"F0.wireOp",EDGE,"E119"),sQuery(id+"F0.wireOp",EDGE,"E120"),sQuery(id+"F0.wireOp",EDGE,"E121"),sQuery(id+"F0.wireOp",EDGE,"E122"),sQuery(id+"F0.wireOp",EDGE,"E123"),sQuery(id+"F0.wireOp",EDGE,"E124"),sQuery(id+"F0.wireOp",EDGE,"E125"),sQuery(id+"F0.wireOp",EDGE,"E126"),sQuery(id+"F0.wireOp",EDGE,"E127"),sQuery(id+"F0.wireOp",EDGE,"E128"),sQuery(id+"F0.wireOp",EDGE,"E129"),sQuery(id+"F0.wireOp",EDGE,"E130"),sQuery(id+"F0.wireOp",EDGE,"E131"),sQuery(id+"F0.wireOp",EDGE,"E132"),sQuery(id+"F0.wireOp",EDGE,"E133"),sQuery(id+"F0.wireOp",EDGE,"E134"),sQuery(id+"F0.wireOp",EDGE,"E135"),sQuery(id+"F0.wireOp",EDGE,"E136"),sQuery(id+"F0.wireOp",EDGE,"E137"),sQuery(id+"F0.wireOp",EDGE,"E138"),sQuery(id+"F0.wireOp",EDGE,"E139"),sQuery(id+"F0.wireOp",EDGE,"E140"),sQuery(id+"F0.wireOp",EDGE,"E141"),sQuery(id+"F0.wireOp",EDGE,"E142"),sQuery(id+"F0.wireOp",EDGE,"E143"),sQuery(id+"F0.wireOp",EDGE,"E144"),sQuery(id+"F0.wireOp",EDGE,"E145"),sQuery(id+"F0.wireOp",EDGE,"E146"),sQuery(id+"F0.wireOp",EDGE,"E147"),sQuery(id+"F0.wireOp",EDGE,"E148"),sQuery(id+"F0.wireOp",EDGE,"E149"),sQuery(id+"F0.wireOp",EDGE,"E150"),sQuery(id+"F0.wireOp",EDGE,"E151"),sQuery(id+"F0.wireOp",EDGE,"E152"),sQuery(id+"F0.wireOp",EDGE,"E153"),sQuery(id+"F0.wireOp",EDGE,"E154"),sQuery(id+"F0.wireOp",EDGE,"E155"),sQuery(id+"F0.wireOp",EDGE,"E156"),sQuery(id+"F0.wireOp",EDGE,"E157"),sQuery(id+"F0.wireOp",EDGE,"E158"),sQuery(id+"F0.wireOp",EDGE,"E159"),sQuery(id+"F0.wireOp",EDGE,"E160"),sQuery(id+"F0.wireOp",EDGE,"E161"),sQuery(id+"F0.wireOp",EDGE,"E162"),sQuery(id+"F0.wireOp",EDGE,"E163"),sQuery(id+"F0.wireOp",EDGE,"E164"),sQuery(id+"F0.wireOp",EDGE,"E165"),sQuery(id+"F0.wireOp",EDGE,"E166"),sQuery(id+"F0.wireOp",EDGE,"E167"),sQuery(id+"F0.wireOp",EDGE,"E168"),sQuery(id+"F0.wireOp",EDGE,"E169"),sQuery(id+"F0.wireOp",EDGE,"E170"),sQuery(id+"F0.wireOp",EDGE,"E171"),sQuery(id+"F0.wireOp",EDGE,"E172"),sQuery(id+"F0.wireOp",EDGE,"E173"),sQuery(id+"F0.wireOp",EDGE,"E174"),sQuery(id+"F0.wireOp",EDGE,"E175"),sQuery(id+"F0.wireOp",EDGE,"E176"),sQuery(id+"F0.wireOp",EDGE,"E177"),sQuery(id+"F0.wireOp",EDGE,"E178"),sQuery(id+"F0.wireOp",EDGE,"E179"),sQuery(id+"F0.wireOp",EDGE,"E180"),sQuery(id+"F0.wireOp",EDGE,"E181")])],"isStart":false}),makeQuery(id+"F5.opExtrude","SWEPT_FACE",FACE,{"disambiguationData":[OSD([sQuery(id+"F4.wireOp",EDGE,"E189.bottom")])]}),makeQuery(id+"F5.opExtrude","SWEPT_FACE",FACE,{"disambiguationData":[OSD([sQuery(id+"F4.wireOp",EDGE,"E192.0.1")])]})]}),makeQuery(id+"F7.opExtrude","SWEPT_FACE",FACE,{"disambiguationData":[OSD([sQuery(id+"F6.wireOp",EDGE,"E193.top")])]})]}),makeQuery(id+"F11.opExtrude","CAP_FACE",FACE,{"disambiguationData":[OSD([sQuery(id+"F10.wireOp",EDGE,"E198.bottom"),sQuery(id+"F10.wireOp",EDGE,"E198.top"),sQuery(id+"F10.wireOp",EDGE,"E198.left"),sQuery(id+"F10.wireOp",EDGE,"E198.right"),sQuery(id+"F10.wireOp",EDGE,"E199")])],"isStart":false})]});
            var sketch = newSketch(context, id + "F12", { "sketchPlane" : qUnion([Q0])});
            skLineSegment(sketch, "E200.bottom", {"start": v(-4.8, -7) * mm, "end": v(4.8, -7) * mm});
            skLineSegment(sketch, "E200.top", {"start": v(-9.8, -22.7) * mm, "end": v(9.8, -22.7) * mm});
            skLineSegment(sketch, "E200.left", {"start": v(-9.8, -12) * mm, "end": v(-9.8, -22.7) * mm});
            skLineSegment(sketch, "E200.right", {"start": v(9.8, -12) * mm, "end": v(9.8, -22.7) * mm});
            skPoint(sketch, "E200.middle", {"position": v(0, -14.85) * mm});
            skPoint(sketch, "E201.visualSharp", {"position": v(-9.8, -7) * mm});
            skArc(sketch, "E201.filletArc", {"start": v(-4.8, -7) * mm, "mid": v(-8.34, -8.46) * mm, "end": v(-9.8, -12) * mm});
            skPoint(sketch, "E202.visualSharp", {"position": v(9.8, -7) * mm});
            skArc(sketch, "E202.filletArc", {"start": v(9.8, -12) * mm, "mid": v(8.34, -8.46) * mm, "end": v(4.8, -7) * mm});
            skLineSegment(sketch, "E203", {"start": v(-9.08, -9.42) * mm, "end": v(9.08, -9.42) * mm});
            skSolve(sketch);
        }
        {
            var Q0;
            {var subQ0=sQuery(id+"F12.wireOp",EDGE,"E201.filletArc");var subQ1=sQuery(id+"F12.wireOp",EDGE,"E200.bottom");var subQ2=makeQuery(id+"F12.imprint","INTERSECT",VERTEX,{"derivedFrom":[subQ1,subQ0]});Q0=makeQuery(id+"F12.imprint","IMPRINT",FACE,{"disambiguationData":[TD([[makeQuery(id+"F12.imprint","IMPRINT",EDGE,{"disambiguationData":[TD([[subQ2,-1.0]])],"derivedFrom":subQ1}),-1.0]])]});}
            var Q1;
            {var subQ0=sQuery(id+"F12.wireOp",EDGE,"E202.filletArc");var subQ1=sQuery(id+"F12.wireOp",EDGE,"E200.bottom");var subQ2=makeQuery(id+"F12.imprint","INTERSECT",VERTEX,{"derivedFrom":[subQ1,subQ0]});Q1=makeQuery(id+"F12.imprint","IMPRINT",FACE,{"disambiguationData":[TD([[makeQuery(id+"F12.imprint","IMPRINT",EDGE,{"disambiguationData":[TD([[subQ2,1.0]])],"derivedFrom":subQ1}),-1.0]])]});}
            extrude(context, id + "F13", {"entities" : qUnion([Q0, Q1]), "operationType" : NewBodyOperationType.REMOVE, "endBound" : BoundingType.UP_TO_NEXT, "oppositeDirection" : true, "depth" : 25 * mm});
        }
        {
            var Q0;
            Q0=makeQuery(id+"F1.opExtrude","SWEPT_BODY",BODY,{"disambiguationData":[OSD([sQuery(id+"F0.wireOp",EDGE,"E0"),sQuery(id+"F0.wireOp",EDGE,"E1"),sQuery(id+"F0.wireOp",EDGE,"E2"),sQuery(id+"F0.wireOp",EDGE,"E3"),sQuery(id+"F0.wireOp",EDGE,"E4"),sQuery(id+"F0.wireOp",EDGE,"E5"),sQuery(id+"F0.wireOp",EDGE,"E6"),sQuery(id+"F0.wireOp",EDGE,"E7"),sQuery(id+"F0.wireOp",EDGE,"E8"),sQuery(id+"F0.wireOp",EDGE,"E9"),sQuery(id+"F0.wireOp",EDGE,"E10"),sQuery(id+"F0.wireOp",EDGE,"E11"),sQuery(id+"F0.wireOp",EDGE,"E12"),sQuery(id+"F0.wireOp",EDGE,"E13"),sQuery(id+"F0.wireOp",EDGE,"E14"),sQuery(id+"F0.wireOp",EDGE,"E15"),sQuery(id+"F0.wireOp",EDGE,"E16"),sQuery(id+"F0.wireOp",EDGE,"E17"),sQuery(id+"F0.wireOp",EDGE,"E18"),sQuery(id+"F0.wireOp",EDGE,"E19"),sQuery(id+"F0.wireOp",EDGE,"E20"),sQuery(id+"F0.wireOp",EDGE,"E21"),sQuery(id+"F0.wireOp",EDGE,"E22"),sQuery(id+"F0.wireOp",EDGE,"E23"),sQuery(id+"F0.wireOp",EDGE,"E24"),sQuery(id+"F0.wireOp",EDGE,"E25"),sQuery(id+"F0.wireOp",EDGE,"E26"),sQuery(id+"F0.wireOp",EDGE,"E27"),sQuery(id+"F0.wireOp",EDGE,"E28"),sQuery(id+"F0.wireOp",EDGE,"E29"),sQuery(id+"F0.wireOp",EDGE,"E30"),sQuery(id+"F0.wireOp",EDGE,"E31"),sQuery(id+"F0.wireOp",EDGE,"E32"),sQuery(id+"F0.wireOp",EDGE,"E33"),sQuery(id+"F0.wireOp",EDGE,"E34"),sQuery(id+"F0.wireOp",EDGE,"E35"),sQuery(id+"F0.wireOp",EDGE,"E36"),sQuery(id+"F0.wireOp",EDGE,"E37"),sQuery(id+"F0.wireOp",EDGE,"E38"),sQuery(id+"F0.wireOp",EDGE,"E39"),sQuery(id+"F0.wireOp",EDGE,"E40"),sQuery(id+"F0.wireOp",EDGE,"E41"),sQuery(id+"F0.wireOp",EDGE,"E42"),sQuery(id+"F0.wireOp",EDGE,"E43"),sQuery(id+"F0.wireOp",EDGE,"E44"),sQuery(id+"F0.wireOp",EDGE,"E45"),sQuery(id+"F0.wireOp",EDGE,"E46"),sQuery(id+"F0.wireOp",EDGE,"E47"),sQuery(id+"F0.wireOp",EDGE,"E48"),sQuery(id+"F0.wireOp",EDGE,"E49"),sQuery(id+"F0.wireOp",EDGE,"E50"),sQuery(id+"F0.wireOp",EDGE,"E51"),sQuery(id+"F0.wireOp",EDGE,"E52"),sQuery(id+"F0.wireOp",EDGE,"E53"),sQuery(id+"F0.wireOp",EDGE,"E54"),sQuery(id+"F0.wireOp",EDGE,"E55"),sQuery(id+"F0.wireOp",EDGE,"E56"),sQuery(id+"F0.wireOp",EDGE,"E57"),sQuery(id+"F0.wireOp",EDGE,"E58"),sQuery(id+"F0.wireOp",EDGE,"E59"),sQuery(id+"F0.wireOp",EDGE,"E60"),sQuery(id+"F0.wireOp",EDGE,"E61"),sQuery(id+"F0.wireOp",EDGE,"E62"),sQuery(id+"F0.wireOp",EDGE,"E63"),sQuery(id+"F0.wireOp",EDGE,"E64"),sQuery(id+"F0.wireOp",EDGE,"E65"),sQuery(id+"F0.wireOp",EDGE,"E66"),sQuery(id+"F0.wireOp",EDGE,"E67"),sQuery(id+"F0.wireOp",EDGE,"E68"),sQuery(id+"F0.wireOp",EDGE,"E69"),sQuery(id+"F0.wireOp",EDGE,"E70"),sQuery(id+"F0.wireOp",EDGE,"E71"),sQuery(id+"F0.wireOp",EDGE,"E72"),sQuery(id+"F0.wireOp",EDGE,"E73"),sQuery(id+"F0.wireOp",EDGE,"E74"),sQuery(id+"F0.wireOp",EDGE,"E75"),sQuery(id+"F0.wireOp",EDGE,"E76"),sQuery(id+"F0.wireOp",EDGE,"E77"),sQuery(id+"F0.wireOp",EDGE,"E78"),sQuery(id+"F0.wireOp",EDGE,"E79"),sQuery(id+"F0.wireOp",EDGE,"E80"),sQuery(id+"F0.wireOp",EDGE,"E81"),sQuery(id+"F0.wireOp",EDGE,"E82"),sQuery(id+"F0.wireOp",EDGE,"E83"),sQuery(id+"F0.wireOp",EDGE,"E84"),sQuery(id+"F0.wireOp",EDGE,"E85"),sQuery(id+"F0.wireOp",EDGE,"E86"),sQuery(id+"F0.wireOp",EDGE,"E87"),sQuery(id+"F0.wireOp",EDGE,"E88"),sQuery(id+"F0.wireOp",EDGE,"E89"),sQuery(id+"F0.wireOp",EDGE,"E90"),sQuery(id+"F0.wireOp",EDGE,"E91"),sQuery(id+"F0.wireOp",EDGE,"E92"),sQuery(id+"F0.wireOp",EDGE,"E93"),sQuery(id+"F0.wireOp",EDGE,"E94"),sQuery(id+"F0.wireOp",EDGE,"E95"),sQuery(id+"F0.wireOp",EDGE,"E96"),sQuery(id+"F0.wireOp",EDGE,"E97"),sQuery(id+"F0.wireOp",EDGE,"E98"),sQuery(id+"F0.wireOp",EDGE,"E99"),sQuery(id+"F0.wireOp",EDGE,"E100"),sQuery(id+"F0.wireOp",EDGE,"E101"),sQuery(id+"F0.wireOp",EDGE,"E102"),sQuery(id+"F0.wireOp",EDGE,"E103"),sQuery(id+"F0.wireOp",EDGE,"E104"),sQuery(id+"F0.wireOp",EDGE,"E105"),sQuery(id+"F0.wireOp",EDGE,"E106"),sQuery(id+"F0.wireOp",EDGE,"E107"),sQuery(id+"F0.wireOp",EDGE,"E108"),sQuery(id+"F0.wireOp",EDGE,"E109"),sQuery(id+"F0.wireOp",EDGE,"E110"),sQuery(id+"F0.wireOp",EDGE,"E111"),sQuery(id+"F0.wireOp",EDGE,"E112"),sQuery(id+"F0.wireOp",EDGE,"E113"),sQuery(id+"F0.wireOp",EDGE,"E114"),sQuery(id+"F0.wireOp",EDGE,"E115"),sQuery(id+"F0.wireOp",EDGE,"E116"),sQuery(id+"F0.wireOp",EDGE,"E117"),sQuery(id+"F0.wireOp",EDGE,"E118"),sQuery(id+"F0.wireOp",EDGE,"E119"),sQuery(id+"F0.wireOp",EDGE,"E120"),sQuery(id+"F0.wireOp",EDGE,"E121"),sQuery(id+"F0.wireOp",EDGE,"E122"),sQuery(id+"F0.wireOp",EDGE,"E123"),sQuery(id+"F0.wireOp",EDGE,"E124"),sQuery(id+"F0.wireOp",EDGE,"E125"),sQuery(id+"F0.wireOp",EDGE,"E126"),sQuery(id+"F0.wireOp",EDGE,"E127"),sQuery(id+"F0.wireOp",EDGE,"E128"),sQuery(id+"F0.wireOp",EDGE,"E129"),sQuery(id+"F0.wireOp",EDGE,"E130"),sQuery(id+"F0.wireOp",EDGE,"E131"),sQuery(id+"F0.wireOp",EDGE,"E132"),sQuery(id+"F0.wireOp",EDGE,"E133"),sQuery(id+"F0.wireOp",EDGE,"E134"),sQuery(id+"F0.wireOp",EDGE,"E135"),sQuery(id+"F0.wireOp",EDGE,"E136"),sQuery(id+"F0.wireOp",EDGE,"E137"),sQuery(id+"F0.wireOp",EDGE,"E138"),sQuery(id+"F0.wireOp",EDGE,"E139"),sQuery(id+"F0.wireOp",EDGE,"E140"),sQuery(id+"F0.wireOp",EDGE,"E141"),sQuery(id+"F0.wireOp",EDGE,"E142"),sQuery(id+"F0.wireOp",EDGE,"E143"),sQuery(id+"F0.wireOp",EDGE,"E144"),sQuery(id+"F0.wireOp",EDGE,"E145"),sQuery(id+"F0.wireOp",EDGE,"E146"),sQuery(id+"F0.wireOp",EDGE,"E147"),sQuery(id+"F0.wireOp",EDGE,"E148"),sQuery(id+"F0.wireOp",EDGE,"E149"),sQuery(id+"F0.wireOp",EDGE,"E150"),sQuery(id+"F0.wireOp",EDGE,"E151"),sQuery(id+"F0.wireOp",EDGE,"E152"),sQuery(id+"F0.wireOp",EDGE,"E153"),sQuery(id+"F0.wireOp",EDGE,"E154"),sQuery(id+"F0.wireOp",EDGE,"E155"),sQuery(id+"F0.wireOp",EDGE,"E156"),sQuery(id+"F0.wireOp",EDGE,"E157"),sQuery(id+"F0.wireOp",EDGE,"E158"),sQuery(id+"F0.wireOp",EDGE,"E159"),sQuery(id+"F0.wireOp",EDGE,"E160"),sQuery(id+"F0.wireOp",EDGE,"E161"),sQuery(id+"F0.wireOp",EDGE,"E162"),sQuery(id+"F0.wireOp",EDGE,"E163"),sQuery(id+"F0.wireOp",EDGE,"E164"),sQuery(id+"F0.wireOp",EDGE,"E165"),sQuery(id+"F0.wireOp",EDGE,"E166"),sQuery(id+"F0.wireOp",EDGE,"E167"),sQuery(id+"F0.wireOp",EDGE,"E168"),sQuery(id+"F0.wireOp",EDGE,"E169"),sQuery(id+"F0.wireOp",EDGE,"E170"),sQuery(id+"F0.wireOp",EDGE,"E171"),sQuery(id+"F0.wireOp",EDGE,"E172"),sQuery(id+"F0.wireOp",EDGE,"E173"),sQuery(id+"F0.wireOp",EDGE,"E174"),sQuery(id+"F0.wireOp",EDGE,"E175"),sQuery(id+"F0.wireOp",EDGE,"E176"),sQuery(id+"F0.wireOp",EDGE,"E177"),sQuery(id+"F0.wireOp",EDGE,"E178"),sQuery(id+"F0.wireOp",EDGE,"E179"),sQuery(id+"F0.wireOp",EDGE,"E180"),sQuery(id+"F0.wireOp",EDGE,"E181")])]});
            var Q1;
            Q1=qCreatedBy(makeId("Right.planeOp"),FACE);
            mirror(context, id + "F14", {"entities" : qUnion([Q0]), "mirrorPlane" : qUnion([Q1])});
        }
    });
